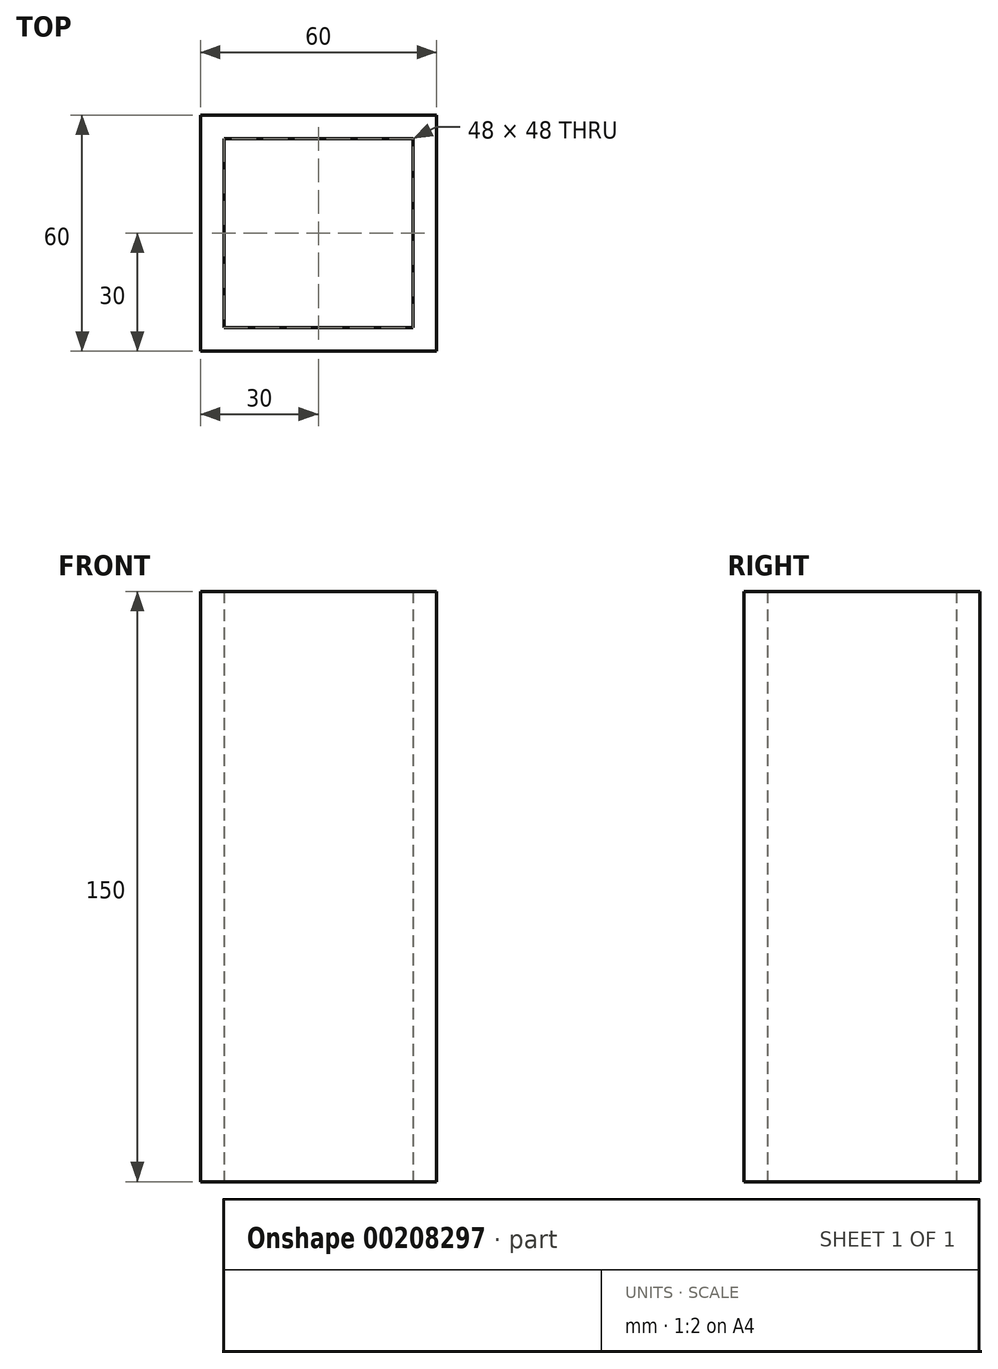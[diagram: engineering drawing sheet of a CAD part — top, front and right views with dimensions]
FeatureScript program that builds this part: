
annotation { "Feature Type Name" : "Feature", "Feature Type Description" : "" }
export const myFeature = defineFeature(function(context is Context, id is Id, definition is map)
    precondition{}
    {
        {
            var Q0;
            Q0=qCreatedBy(makeId("Top.planeOp"),FACE);
            var sketch = newSketch(context, id + "F0", { "sketchPlane" : qUnion([Q0])});
            skLineSegment(sketch, "E0.bottom", {"start": v(30, 30) * mm, "end": v(-30, 30) * mm});
            skLineSegment(sketch, "E0.top", {"start": v(30, -30) * mm, "end": v(-30, -30) * mm});
            skLineSegment(sketch, "E0.left", {"start": v(30, 30) * mm, "end": v(30, -30) * mm});
            skLineSegment(sketch, "E0.right", {"start": v(-30, 30) * mm, "end": v(-30, -30) * mm});
            skPoint(sketch, "E0.middle", {"position": v(0, 0) * mm});
            skSolve(sketch);
        }
        {
            var Q0;
            Q0 = qSketchRegion(id + "F0", true);
            extrude(context, id + "F1", {"entities" : qUnion([Q0]), "depth" : 150 * mm});
        }
        {
            var Q0;
            Q0=qCreatedBy(makeId("Top.planeOp"),FACE);
            var sketch = newSketch(context, id + "F2", { "sketchPlane" : qUnion([Q0])});
            skLineSegment(sketch, "E1.bottom", {"start": v(24, 24) * mm, "end": v(-24, 24) * mm});
            skLineSegment(sketch, "E1.top", {"start": v(24, -24) * mm, "end": v(-24, -24) * mm});
            skLineSegment(sketch, "E1.left", {"start": v(24, 24) * mm, "end": v(24, -24) * mm});
            skLineSegment(sketch, "E1.right", {"start": v(-24, 24) * mm, "end": v(-24, -24) * mm});
            skPoint(sketch, "E1.middle", {"position": v(0, 0) * mm});
            skSolve(sketch);
        }
        {
            var Q0;
            Q0 = qSketchRegion(id + "F2", true);
            extrude(context, id + "F3", {"entities" : qUnion([Q0]), "operationType" : NewBodyOperationType.REMOVE, "depth" : 150 * mm});
        }
    });
